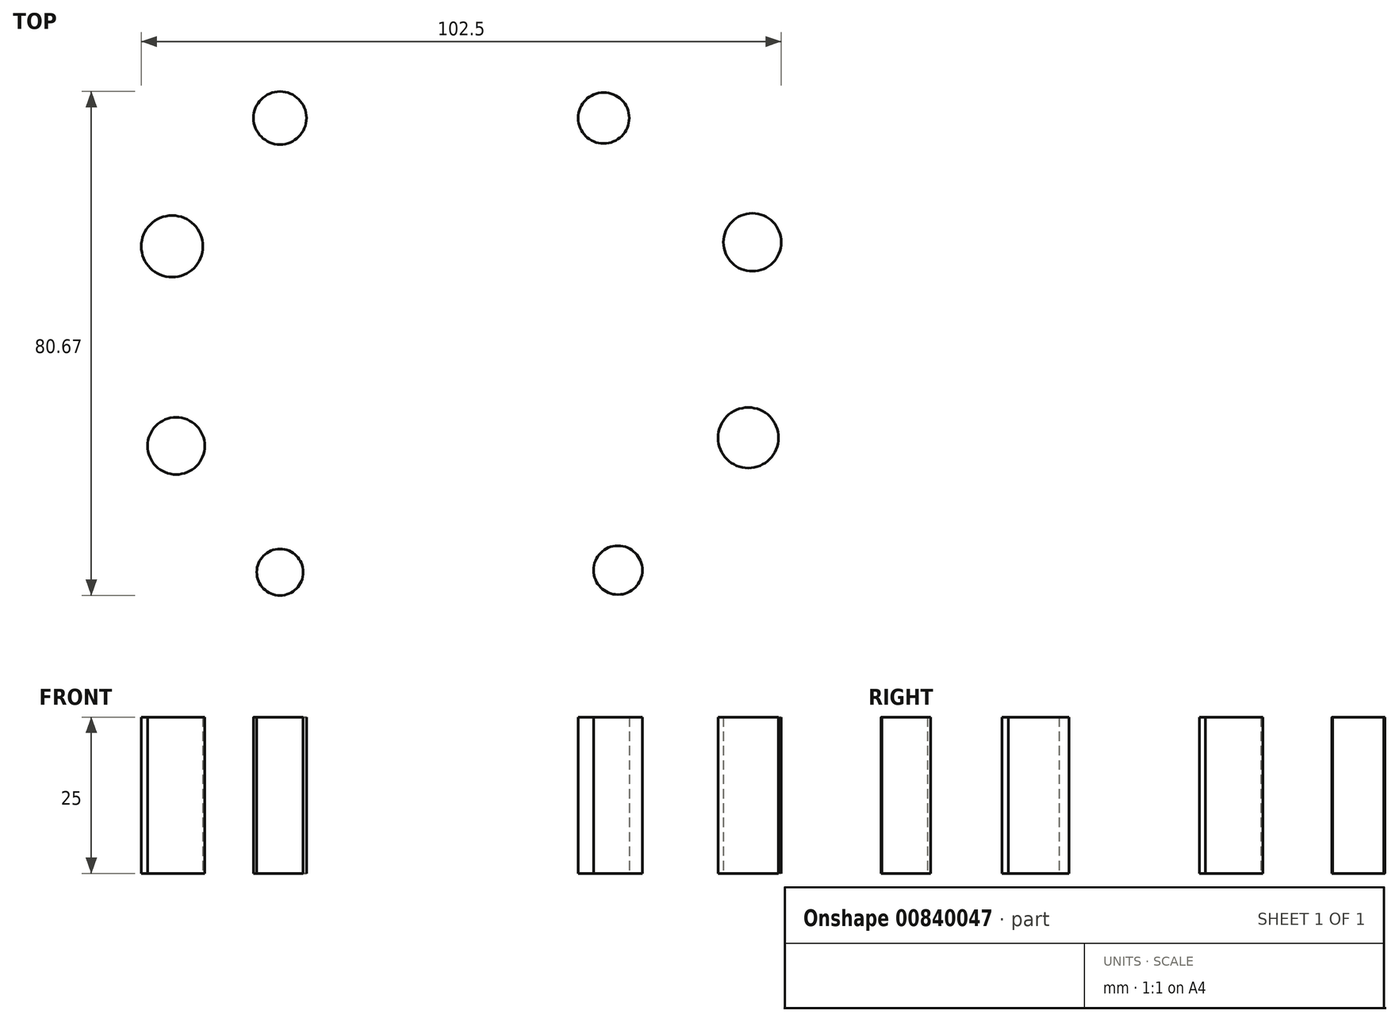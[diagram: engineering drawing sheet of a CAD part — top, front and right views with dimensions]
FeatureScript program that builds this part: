
annotation { "Feature Type Name" : "Feature", "Feature Type Description" : "" }
export const myFeature = defineFeature(function(context is Context, id is Id, definition is map)
    precondition{}
    {
        {
            var Q0;
            Q0=qCreatedBy(makeId("Top.planeOp"),FACE);
            var sketch = newSketch(context, id + "F0", { "sketchPlane" : qUnion([Q0])});
            skLineSegment(sketch, "E0", {"start": v(-57.55, 39.78) * mm, "end": v(46.8, 39.78) * mm});
            skLineSegment(sketch, "E1", {"start": v(46.8, 39.78) * mm, "end": v(46.8, -41.41) * mm});
            skLineSegment(sketch, "E2", {"start": v(46.8, -41.41) * mm, "end": v(-57.55, -41.41) * mm});
            skLineSegment(sketch, "E3", {"start": v(-57.55, -41.41) * mm, "end": v(-57.55, 39.78) * mm});
            skLineSegment(sketch, "E4", {"start": v(46.8, 39.78) * mm, "end": v(35.05, 31.63) * mm});
            skLineSegment(sketch, "E5", {"start": v(35.05, 31.63) * mm, "end": v(35.05, -32.6) * mm});
            skLineSegment(sketch, "E6", {"start": v(35.05, -32.6) * mm, "end": v(46.8, -41.41) * mm});
            skLineSegment(sketch, "E7", {"start": v(35.05, -32.6) * mm, "end": v(-45.49, -32.6) * mm});
            skLineSegment(sketch, "E8", {"start": v(-45.49, -32.6) * mm, "end": v(-57.55, -41.41) * mm});
            skLineSegment(sketch, "E9", {"start": v(-45.49, -32.6) * mm, "end": v(-45.49, 31.3) * mm});
            skLineSegment(sketch, "E10", {"start": v(-45.49, 31.3) * mm, "end": v(-57.55, 39.78) * mm});
            skLineSegment(sketch, "E11", {"start": v(-45.49, 31.3) * mm, "end": v(35.05, 31.63) * mm});
            skSolve(sketch);
        }
        {
            var Q0;
            Q0=makeQuery(id+"F0.imprint","IMPRINT",FACE,{"disambiguationData":[TD([[makeQuery(id+"F0.imprint","IMPRINT",EDGE,{"derivedFrom":sQuery(id+"F0.wireOp",EDGE,"E5")}),-1.0]])]});
            var sketch = newSketch(context, id + "F1", { "sketchPlane" : qUnion([Q0])});
            skCircle(sketch, "E12", {"center": v(-34.4, 35.54) * mm, "radius": 4.24 * mm});
            skCircle(sketch, "E13", {"center": v(17.45, 35.54) * mm, "radius": 4.09 * mm});
            skCircle(sketch, "E14", {"center": v(41.25, 15.65) * mm, "radius": 4.63 * mm});
            skCircle(sketch, "E15", {"center": v(40.6, -15.65) * mm, "radius": 4.85 * mm});
            skCircle(sketch, "E16", {"center": v(19.73, -36.85) * mm, "radius": 3.91 * mm});
            skCircle(sketch, "E17", {"center": v(-34.4, -37.17) * mm, "radius": 3.72 * mm});
            skCircle(sketch, "E18", {"center": v(-51.03, -16.96) * mm, "radius": 4.58 * mm});
            skCircle(sketch, "E19", {"center": v(-51.68, 15) * mm, "radius": 4.93 * mm});
            skSolve(sketch);
        }
        {
            var Q0;
            Q0 = qSketchRegion(id + "F1", true);
            extrude(context, id + "F2", {"entities" : qUnion([Q0]), "depth" : 25 * mm, "offsetDistance" : 25 * mm});
        }
    });
